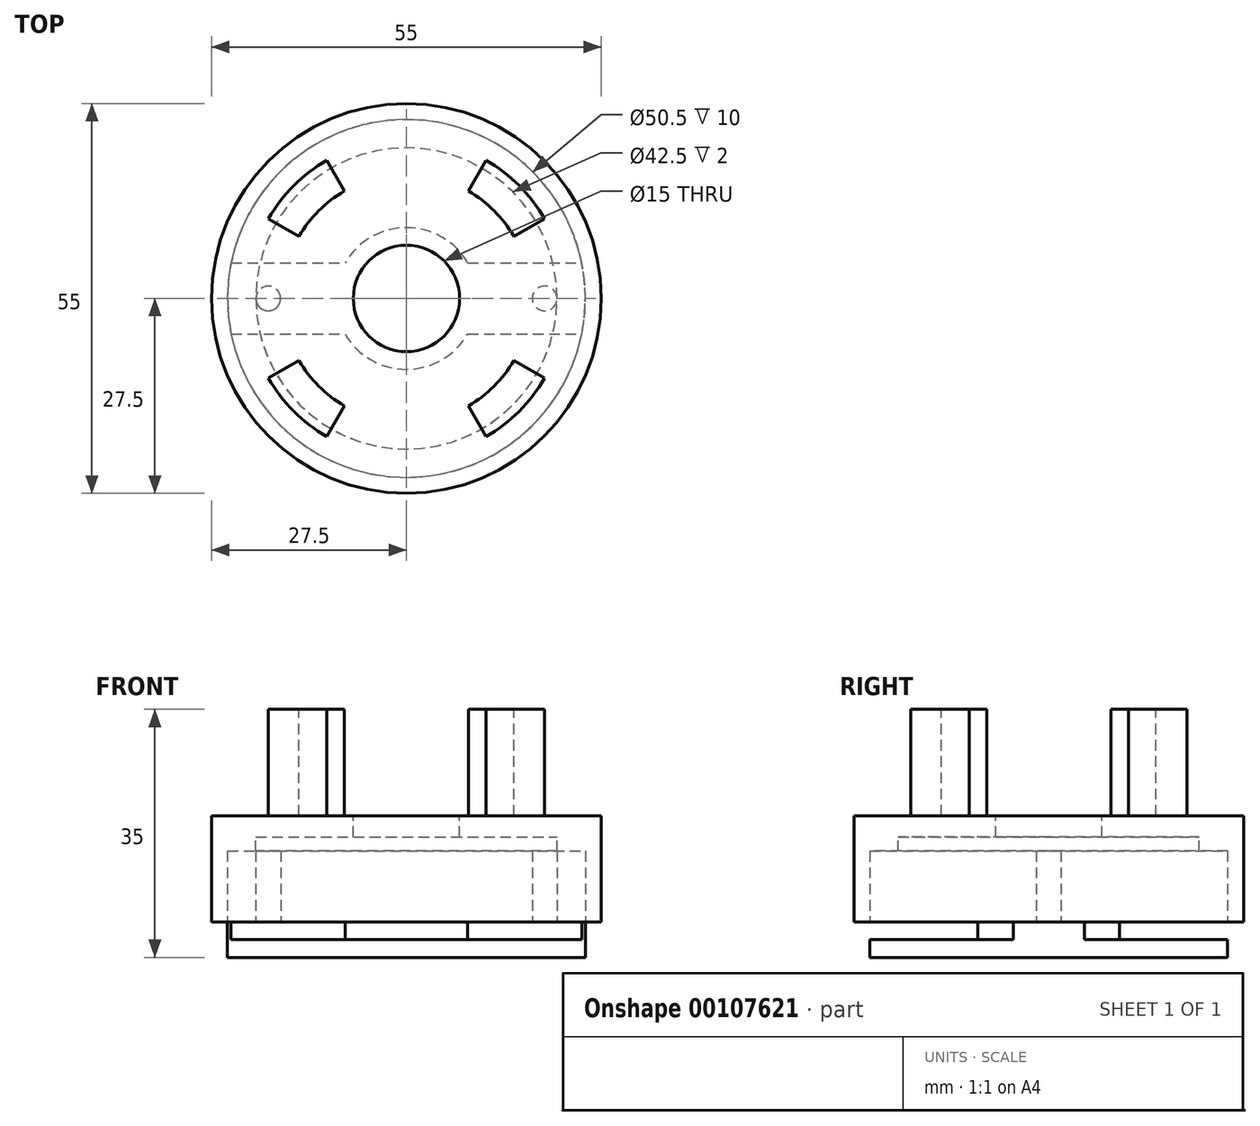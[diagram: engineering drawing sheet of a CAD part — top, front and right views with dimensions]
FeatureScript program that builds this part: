
annotation { "Feature Type Name" : "Feature", "Feature Type Description" : "" }
export const myFeature = defineFeature(function(context is Context, id is Id, definition is map)
    precondition{}
    {
        {
            var Q0;
            Q0=qCreatedBy(makeId("Top.planeOp"),FACE);
            var sketch = newSketch(context, id + "F0", { "sketchPlane" : qUnion([Q0])});
            skCircle(sketch, "E0", {"center": v(0, 0) * mm, "radius": 27.5 * mm});
            skSolve(sketch);
        }
        {
            var Q0;
            Q0 = qSketchRegion(id + "F0", true);
            extrude(context, id + "F1", {"entities" : qUnion([Q0]), "depth" : 15 * mm});
        }
        {
            var Q0;
            Q0=makeQuery(id+"F1.opExtrude","CAP_FACE",FACE,{"disambiguationData":[OSD([sQuery(id+"F0.wireOp",EDGE,"E0")])],"isStart":true});
            var sketch = newSketch(context, id + "F2", { "sketchPlane" : qUnion([Q0])});
            skCircle(sketch, "E1", {"center": v(0, 0) * mm, "radius": 25.25 * mm});
            skSolve(sketch);
        }
        {
            var Q0;
            Q0 = qSketchRegion(id + "F2", true);
            extrude(context, id + "F3", {"entities" : qUnion([Q0]), "operationType" : NewBodyOperationType.REMOVE, "oppositeDirection" : true, "depth" : 12 * mm});
        }
        {
            var Q0;
            Q0=makeQuery(id+"F3.boolean.opBoolean","COPY",FACE,{"derivedFrom":makeQuery(id+"F3.opExtrude","CAP_FACE",FACE,{"disambiguationData":[OSD([sQuery(id+"F2.wireOp",EDGE,"E1")])],"isStart":false})});
            var sketch = newSketch(context, id + "F4", { "sketchPlane" : qUnion([Q0])});
            skCircle(sketch, "E2.0", {"center": v(0, 0) * mm, "radius": 25.25 * mm});
            skCircle(sketch, "E3", {"center": v(0, 0) * mm, "radius": 21.25 * mm});
            skSolve(sketch);
        }
        {
            var Q0;
            Q0 = qSketchRegion(id + "F4", true);
            extrude(context, id + "F5", {"entities" : qUnion([Q0]), "operationType" : NewBodyOperationType.ADD, "depth" : 2 * mm});
        }
        {
            var Q0;
            Q0=makeQuery(id+"F1.opExtrude","CAP_FACE",FACE,{"disambiguationData":[OSD([sQuery(id+"F0.wireOp",EDGE,"E0")])],"isStart":false});
            var sketch = newSketch(context, id + "F6", { "sketchPlane" : qUnion([Q0])});
            skCircle(sketch, "E4", {"center": v(0, 0) * mm, "radius": 7.5 * mm});
            skSolve(sketch);
        }
        {
            var Q0;
            Q0 = qSketchRegion(id + "F6", true);
            extrude(context, id + "F7", {"entities" : qUnion([Q0]), "operationType" : NewBodyOperationType.REMOVE, "endBound" : BoundingType.UP_TO_NEXT, "oppositeDirection" : true, "depth" : 25 * mm});
        }
        {
            var Q0;
            Q0=makeQuery(id+"F1.opExtrude","CAP_FACE",FACE,{"disambiguationData":[OSD([sQuery(id+"F0.wireOp",EDGE,"E0")])],"isStart":false});
            var sketch = newSketch(context, id + "F8", { "sketchPlane" : qUnion([Q0])});
            skCircle(sketch, "E5", {"center": v(0, 0) * mm, "radius": 22.5 * mm});
            skCircle(sketch, "E6", {"center": v(0, 0) * mm, "radius": 17.5 * mm});
            skSolve(sketch);
        }
        {
            var Q0;
            Q0 = qSketchRegion(id + "F8", true);
            extrude(context, id + "F9", {"entities" : qUnion([Q0]), "operationType" : NewBodyOperationType.ADD, "depth" : 15 * mm});
        }
        {
            var Q0;
            Q0=makeQuery(id+"F9.opExtrude","CAP_FACE",FACE,{"disambiguationData":[OSD([sQuery(id+"F8.wireOp",EDGE,"E5"),sQuery(id+"F8.wireOp",EDGE,"E6")])],"isStart":false});
            var sketch = newSketch(context, id + "F10", { "sketchPlane" : qUnion([Q0])});
            skArc(sketch, "E7.0", {"start": v(8.75, 15.16) * mm, "mid": v(0, 17.5) * mm, "end": v(-8.75, 15.16) * mm});
            skArc(sketch, "E8.0", {"start": v(11.25, 19.49) * mm, "mid": v(0, 22.5) * mm, "end": v(-11.25, 19.49) * mm});
            skLineSegment(sketch, "E9", {"start": v(8.75, 15.16) * mm, "end": v(11.25, 19.49) * mm});
            skLineSegment(sketch, "E10", {"start": v(-8.75, 15.16) * mm, "end": v(-11.25, 19.49) * mm});
            skLineSegment(sketch, "E11", {"start": v(0, 42.89) * mm, "end": v(0, -58.77) * mm, "construction": true});
            skLineSegment(sketch, "E12.1.0", {"start": v(-15.16, -8.75) * mm, "end": v(-19.49, -11.25) * mm});
            skArc(sketch, "E12.1.1", {"start": v(-15.16, 8.75) * mm, "mid": v(-17.5, 0) * mm, "end": v(-15.16, -8.75) * mm});
            skLineSegment(sketch, "E12.1.2", {"start": v(-15.16, 8.75) * mm, "end": v(-19.49, 11.25) * mm});
            skArc(sketch, "E12.1.3", {"start": v(-19.49, 11.25) * mm, "mid": v(-22.5, 0) * mm, "end": v(-19.49, -11.25) * mm});
            skLineSegment(sketch, "E12.2.0", {"start": v(8.75, -15.16) * mm, "end": v(11.25, -19.49) * mm});
            skArc(sketch, "E12.2.1", {"start": v(-8.75, -15.16) * mm, "mid": v(0, -17.5) * mm, "end": v(8.75, -15.16) * mm});
            skLineSegment(sketch, "E12.2.2", {"start": v(-8.75, -15.16) * mm, "end": v(-11.25, -19.49) * mm});
            skArc(sketch, "E12.2.3", {"start": v(-11.25, -19.49) * mm, "mid": v(0, -22.5) * mm, "end": v(11.25, -19.49) * mm});
            skLineSegment(sketch, "E12.3.0", {"start": v(15.16, 8.75) * mm, "end": v(19.49, 11.25) * mm});
            skArc(sketch, "E12.3.1", {"start": v(15.16, -8.75) * mm, "mid": v(17.5, 0) * mm, "end": v(15.16, 8.75) * mm});
            skLineSegment(sketch, "E12.3.2", {"start": v(15.16, -8.75) * mm, "end": v(19.49, -11.25) * mm});
            skArc(sketch, "E12.3.3", {"start": v(19.49, -11.25) * mm, "mid": v(22.5, 0) * mm, "end": v(19.49, 11.25) * mm});
            skSolve(sketch);
        }
        {
            var Q0;
            Q0=makeQuery(id+"F10.imprint","IMPRINT",FACE,{"disambiguationData":[TD([[makeQuery(id+"F10.imprint","IMPRINT",EDGE,{"derivedFrom":sQuery(id+"F10.wireOp",EDGE,"E12.1.0")}),-1.0]])]});
            var Q1;
            Q1=makeQuery(id+"F10.imprint","IMPRINT",FACE,{"disambiguationData":[TD([[makeQuery(id+"F10.imprint","IMPRINT",EDGE,{"derivedFrom":sQuery(id+"F10.wireOp",EDGE,"E12.2.0")}),-1.0]])]});
            var Q2;
            Q2=makeQuery(id+"F10.imprint","IMPRINT",FACE,{"disambiguationData":[TD([[makeQuery(id+"F10.imprint","IMPRINT",EDGE,{"derivedFrom":sQuery(id+"F10.wireOp",EDGE,"E12.3.0")}),-1.0]])]});
            var Q3;
            Q3=makeQuery(id+"F10.imprint","IMPRINT",FACE,{"disambiguationData":[TD([[makeQuery(id+"F10.imprint","IMPRINT",EDGE,{"derivedFrom":sQuery(id+"F10.wireOp",EDGE,"E7.0")}),-1.0]])]});
            var Q4;
            {var subQ0=sQuery(id+"F0.wireOp",EDGE,"E0");Q4=makeQuery(id+"F9.boolean.opBoolean","SPLIT",FACE,{"disambiguationData":[TD([makeQuery(id+"F1.opExtrude","SWEPT_FACE",FACE,{"disambiguationData":[OSD([subQ0])]})])],"derivedFrom":makeQuery(id+"F1.opExtrude","CAP_FACE",FACE,{"disambiguationData":[OSD([subQ0])],"isStart":false})});}
            extrude(context, id + "F11", {"entities" : qUnion([Q0, Q1, Q2, Q3]), "operationType" : NewBodyOperationType.REMOVE, "endBound" : BoundingType.UP_TO_SURFACE, "oppositeDirection" : true, "endBoundEntityFace" : qUnion([Q4]), "depth" : 25 * mm});
        }
        {
            var Q0;
            Q0=qCreatedBy(makeId("Top.planeOp"),FACE);
            var sketch = newSketch(context, id + "F12", { "sketchPlane" : qUnion([Q0])});
            skArc(sketch, "E13", {"start": v(-8.66, -5) * mm, "mid": v(0, -10) * mm, "end": v(8.66, -5) * mm});
            skLineSegment(sketch, "E14.bottom", {"start": v(-24.75, 5) * mm, "end": v(-8.66, 5) * mm});
            skLineSegment(sketch, "E14.top", {"start": v(-24.75, -5) * mm, "end": v(-8.66, -5) * mm});
            skLineSegment(sketch, "E15", {"start": v(0, -35.37) * mm, "end": v(0, 29.98) * mm, "construction": true});
            skLineSegment(sketch, "E16", {"start": v(52.09, 0) * mm, "end": v(-42.65, 0) * mm, "construction": true});
            skArc(sketch, "E17.0", {"start": v(24.75, -5) * mm, "mid": v(25.25, 0) * mm, "end": v(24.75, 5) * mm});
            skArc(sketch, "E18.trimOffspring", {"start": v(-24.75, 5) * mm, "mid": v(-25.25, 0) * mm, "end": v(-24.75, -5) * mm});
            skLineSegment(sketch, "E19.trimOffspring", {"start": v(8.66, 5) * mm, "end": v(24.75, 5) * mm});
            skLineSegment(sketch, "E20.trimOffspring", {"start": v(8.66, -5) * mm, "end": v(24.75, -5) * mm});
            skArc(sketch, "E21.trimOffspring", {"start": v(8.66, 5) * mm, "mid": v(0, 10) * mm, "end": v(-8.66, 5) * mm});
            skSolve(sketch);
        }
        {
            var Q0;
            Q0 = qSketchRegion(id + "F12", true);
            extrude(context, id + "F13", {"entities" : qUnion([Q0]), "oppositeDirection" : true, "depth" : 2.5 * mm});
        }
        {
            var Q0;
            Q0=makeQuery(id+"F12.imprint","IMPRINT",FACE,{"disambiguationData":[TD([[makeQuery(id+"F12.imprint","IMPRINT",EDGE,{"derivedFrom":sQuery(id+"F12.wireOp",EDGE,"E13")}),1.0]])]});
            var sketch = newSketch(context, id + "F14", { "sketchPlane" : qUnion([Q0])});
            skCircle(sketch, "E22", {"center": v(-19.5, 0) * mm, "radius": 1.75 * mm});
            skCircle(sketch, "E23.MirrorC", {"center": v(19.5, 0) * mm, "radius": 1.75 * mm});
            skSolve(sketch);
        }
        {
            var Q0;
            Q0 = qSketchRegion(id + "F14", true);
            extrude(context, id + "F15", {"entities" : qUnion([Q0]), "operationType" : NewBodyOperationType.ADD, "depth" : 10 * mm});
        }
        {
            var Q0;
            Q0=makeQuery(id+"F13.opExtrude","CAP_FACE",FACE,{"disambiguationData":[OSD([sQuery(id+"F12.wireOp",EDGE,"E13"),sQuery(id+"F12.wireOp",EDGE,"E14.bottom"),sQuery(id+"F12.wireOp",EDGE,"E14.top"),sQuery(id+"F12.wireOp",EDGE,"E17.0"),sQuery(id+"F12.wireOp",EDGE,"E18.trimOffspring"),sQuery(id+"F12.wireOp",EDGE,"E19.trimOffspring"),sQuery(id+"F12.wireOp",EDGE,"E20.trimOffspring"),sQuery(id+"F12.wireOp",EDGE,"E21.trimOffspring")])],"isStart":false});
            var sketch = newSketch(context, id + "F16", { "sketchPlane" : qUnion([Q0])});
            skCircle(sketch, "E24.0", {"center": v(0, 0) * mm, "radius": 25.25 * mm});
            skSolve(sketch);
        }
        {
            var Q0;
            Q0 = qSketchRegion(id + "F16", true);
            extrude(context, id + "F17", {"entities" : qUnion([Q0]), "operationType" : NewBodyOperationType.ADD, "depth" : 2.5 * mm});
        }
    });
